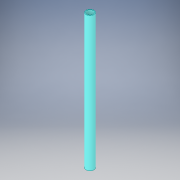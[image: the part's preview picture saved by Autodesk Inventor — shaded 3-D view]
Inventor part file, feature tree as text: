
AUTODESK INVENTOR PART (.ipt)
format: ipt  version: 2018 (Build 220112000, 112)  size: 104,960 bytes
history: native  units: in
note: dims shown in document units (in); Inventor stores cm internally (conversion verified against a paired STEP export)
features: extrude x1, sketch x1
ambient origin geometry x8: Origin, YZ Plane, XZ Plane, XY Plane, X Axis, Y Axis, Z Axis, Center Point
bodies: Solid1 (feature_tree)
feature tree (2):
  extrude  "Extrusion1"  Depth=6.329in
  sketch  "Sketch1"  dims[d0=0.375in d1=0.31in d2=6.329in d3=0.0in]
